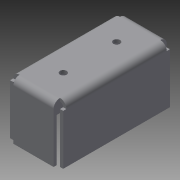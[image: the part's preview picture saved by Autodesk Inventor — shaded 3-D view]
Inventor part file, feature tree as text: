
AUTODESK INVENTOR PART (.ipt)
format: ipt  version: 2013 (Build 170138000, 138)  size: 226,816 bytes
history: native  units: in
note: dims shown in document units (in); Inventor stores cm internally (conversion verified against a paired STEP export)
features: sheet_metal_op x7, sketch x5, other x5, mirror x1, hole x1
ambient origin geometry x8: Origin, YZ Plane, XZ Plane, XY Plane, X Axis, Y Axis, Z Axis, Center Point
bodies: Solid1 (feature_tree)
feature tree (19):
  sheet_metal_op  "Face1"
  sheet_metal_op  "Face2"
  sheet_metal_op  "Face3"
  sheet_metal_op  "Face4"
  mirror  "Mirror5"
  hole  "Hole3"  [1 undecoded]
  sketch  "Sketch1"  dims[d0=0.875in d1=4.0in]
  other  "Plate1"
  sketch  "Sketch10"  dims[d2=0.12in]
  other  "Plate5"
  sheet_metal_op  "Bend4"
  sketch  "Sketch11"  dims[d70=2.0in]
  other  "Plate6"
  sheet_metal_op  "Bend5"
  sketch  "Sketch12"  dims[d72=0.12in]
  other  "Plate7"
  sheet_metal_op  "Bend6"
  sketch  "Sketch13"  dims[d73=0.12in d74=0.06in d75=0.24in d76=0.12in d77=0.12in d78=0.12in d79=0.06in d80=0.24in d81=0.12in d82=0.12in d83=0.12in d84=0.06in d85=0.24in d86=0.12in d88=2.0in d90=0.88in d91=0.88in d92=0.25in d93=0.75in d94=0.375in d95=0.25in d96=0.5635in d97=0.12in d98=0.8108in d99=0.755in d100=0.755in]
  other  "Definition1"
note: 1 required parameter value undecoded (feature->parameter linkage not recoverable at this tier; creation-order binding heuristic only, values carry confidence <= 0.55)
